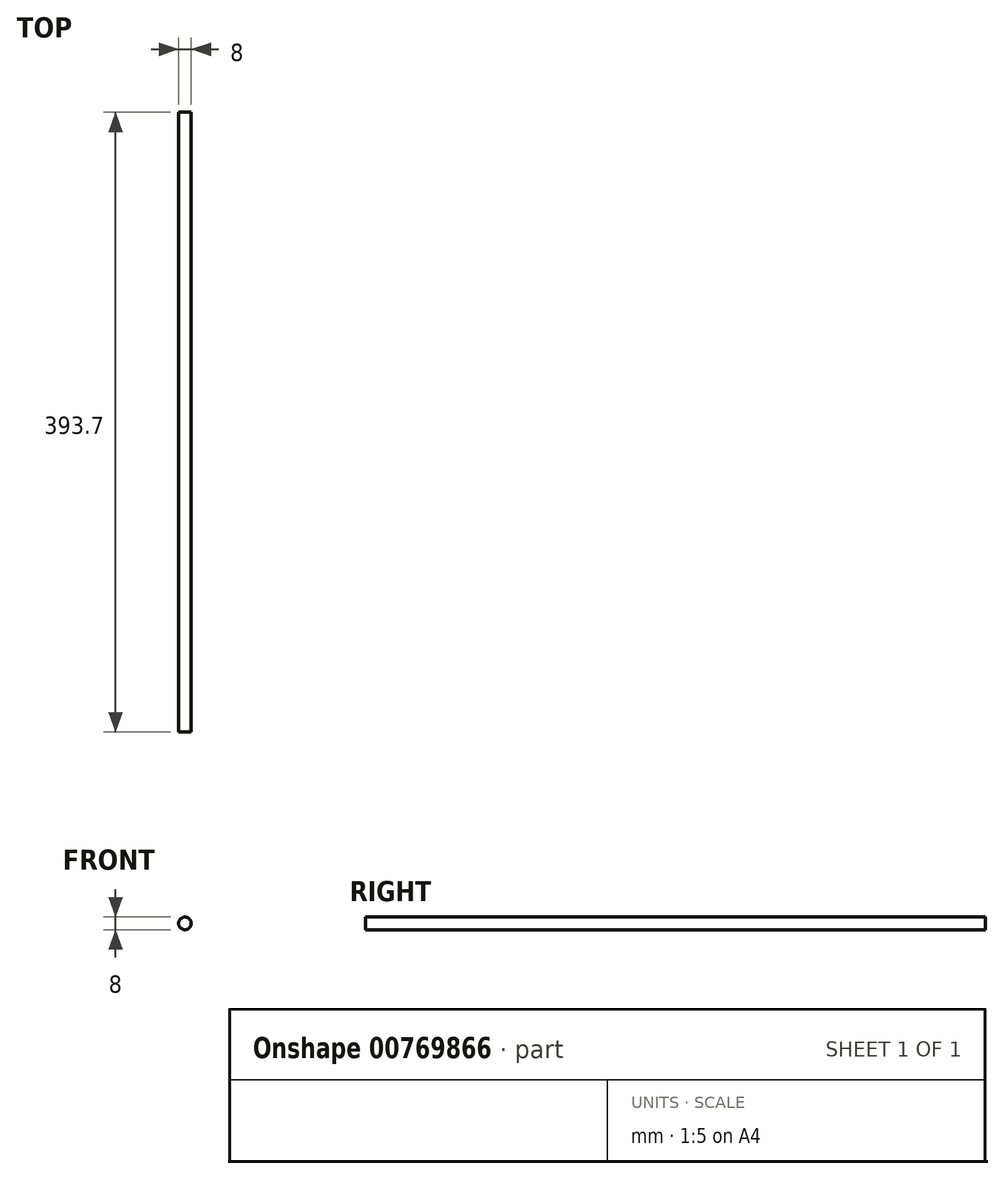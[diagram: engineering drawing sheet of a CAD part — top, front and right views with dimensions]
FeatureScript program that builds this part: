
annotation { "Feature Type Name" : "Feature", "Feature Type Description" : "" }
export const myFeature = defineFeature(function(context is Context, id is Id, definition is map)
    precondition{}
    {
        {
            var Q0;
            Q0=qCreatedBy(makeId("Front.planeOp"),FACE);
            var sketch = newSketch(context, id + "F0", { "sketchPlane" : qUnion([Q0])});
            skCircle(sketch, "E0", {"center": v(0, 0) * mm, "radius": 4 * mm});
            skSolve(sketch);
        }
        {
            var Q0;
            Q0 = qSketchRegion(id + "F0", true);
            extrude(context, id + "F1", {"entities" : qUnion([Q0]), "depth" : 393.7 * mm, "offsetDistance" : 25.4 * mm});
        }
    });
